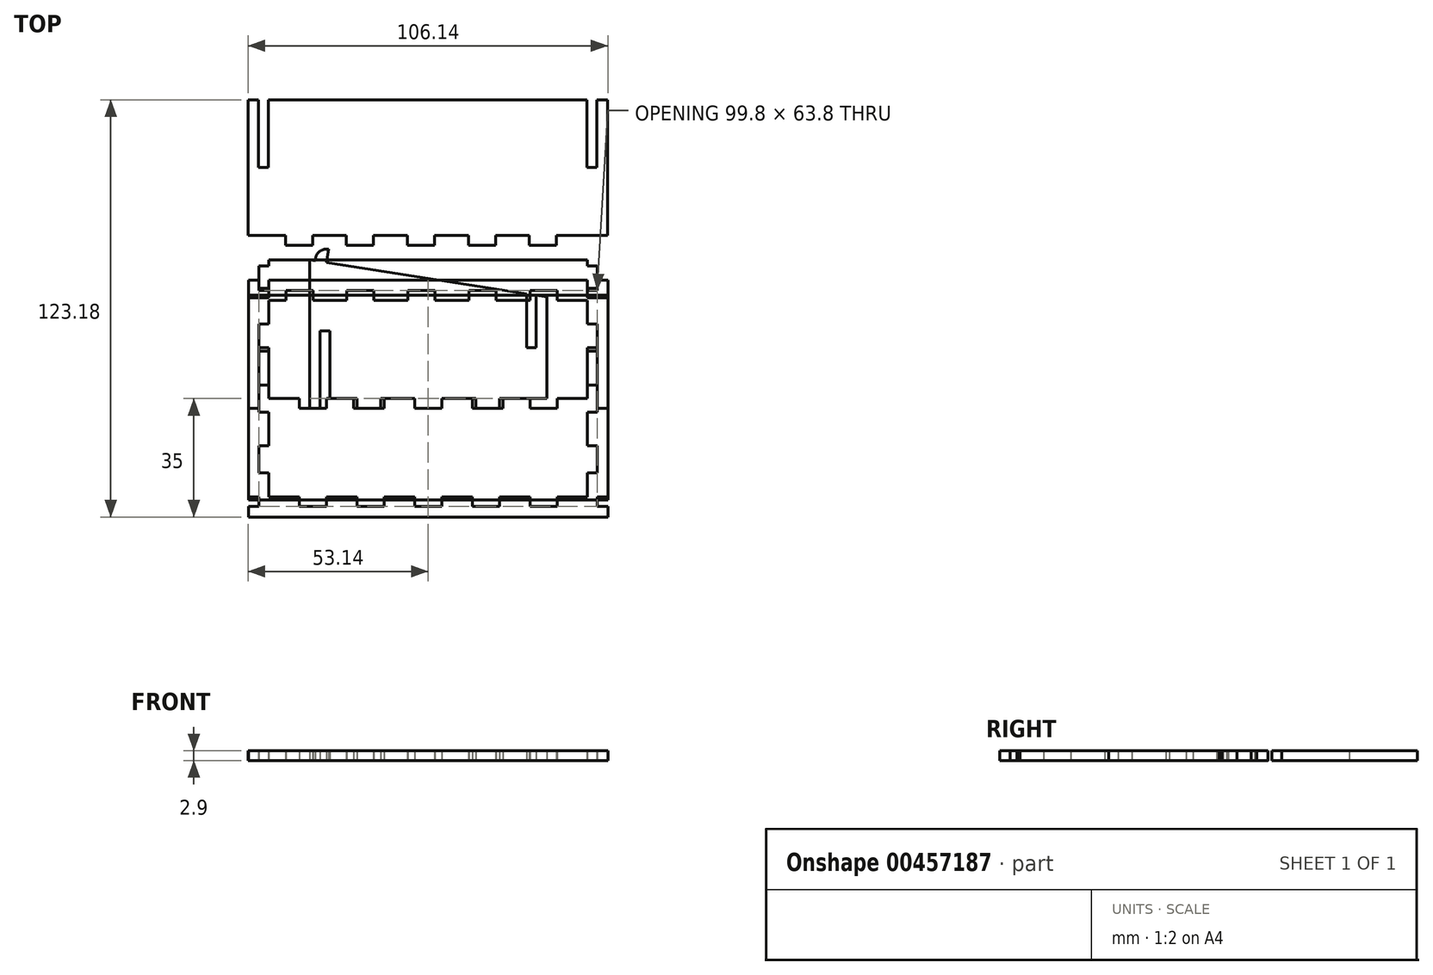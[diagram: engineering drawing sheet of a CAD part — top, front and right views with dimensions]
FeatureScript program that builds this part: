
annotation { "Feature Type Name" : "Feature", "Feature Type Description" : "" }
export const myFeature = defineFeature(function(context is Context, id is Id, definition is map)
    precondition{}
    {
        {
            assignVariable(context, id + "F0", {"name" : "b_thickness", "anyValue" : 2.9});
        }
        {
            var Q0;
            Q0=qCreatedBy(makeId("Top.planeOp"),FACE);
            var sketch = newSketch(context, id + "F1", { "sketchPlane" : qUnion([Q0])});
            skLineSegment(sketch, "E0", {"start": v(47, 29) * mm, "end": v(-47, 29) * mm});
            skLineSegment(sketch, "E1", {"start": v(-47, 29) * mm, "end": v(-47, -29) * mm});
            skLineSegment(sketch, "E2", {"start": v(-47, -29) * mm, "end": v(47, -29) * mm});
            skLineSegment(sketch, "E3", {"start": v(47, -29) * mm, "end": v(47, 29) * mm});
            skLineSegment(sketch, "E4", {"start": v(47, 29) * mm, "end": v(-47, -29) * mm});
            skLineSegment(sketch, "E5", {"start": v(-47, 29) * mm, "end": v(47, -29) * mm});
            skLineSegment(sketch, "E6", {"start": v(-47, 22) * mm, "end": v(-49.9, 22) * mm});
            skLineSegment(sketch, "E7", {"start": v(-49.9, 22) * mm, "end": v(-49.9, 14) * mm});
            skLineSegment(sketch, "E8", {"start": v(-49.9, 14) * mm, "end": v(-47, 14) * mm});
            skLineSegment(sketch, "E9", {"start": v(-47, 14) * mm, "end": v(-47, 22) * mm});
            skLineSegment(sketch, "E10", {"start": v(-47, -4) * mm, "end": v(-47, 4) * mm});
            skLineSegment(sketch, "E11", {"start": v(-47, 4) * mm, "end": v(-49.9, 4) * mm});
            skLineSegment(sketch, "E12", {"start": v(-49.9, 4) * mm, "end": v(-49.9, -4) * mm});
            skLineSegment(sketch, "E13", {"start": v(-49.9, -4) * mm, "end": v(-47, -4) * mm});
            skLineSegment(sketch, "E14", {"start": v(-47, -22) * mm, "end": v(-47, -14) * mm});
            skLineSegment(sketch, "E15", {"start": v(-47, -14) * mm, "end": v(-49.9, -14) * mm});
            skLineSegment(sketch, "E16", {"start": v(-49.9, -14) * mm, "end": v(-49.9, -22) * mm});
            skLineSegment(sketch, "E17", {"start": v(-49.9, -22) * mm, "end": v(-47, -22) * mm});
            skLineSegment(sketch, "E18", {"start": v(47, -14) * mm, "end": v(47, -22) * mm});
            skLineSegment(sketch, "E19", {"start": v(47, -22) * mm, "end": v(49.9, -22) * mm});
            skLineSegment(sketch, "E20", {"start": v(49.9, -22) * mm, "end": v(49.9, -14) * mm});
            skLineSegment(sketch, "E21", {"start": v(49.9, -14) * mm, "end": v(47, -14) * mm});
            skLineSegment(sketch, "E22", {"start": v(47, 4) * mm, "end": v(47, -4) * mm});
            skLineSegment(sketch, "E23", {"start": v(47, -4) * mm, "end": v(49.9, -4) * mm});
            skLineSegment(sketch, "E24", {"start": v(49.9, -4) * mm, "end": v(49.9, 4) * mm});
            skLineSegment(sketch, "E25", {"start": v(49.9, 4) * mm, "end": v(47, 4) * mm});
            skLineSegment(sketch, "E26", {"start": v(47, 22) * mm, "end": v(47, 14) * mm});
            skLineSegment(sketch, "E27", {"start": v(47, 14) * mm, "end": v(49.9, 14) * mm});
            skLineSegment(sketch, "E28", {"start": v(49.9, 14) * mm, "end": v(49.9, 22) * mm});
            skLineSegment(sketch, "E29", {"start": v(49.9, 22) * mm, "end": v(47, 22) * mm});
            skLineSegment(sketch, "E30", {"start": v(-30, -29) * mm, "end": v(-38, -29) * mm});
            skLineSegment(sketch, "E31", {"start": v(-38, -29) * mm, "end": v(-38, -31.9) * mm});
            skLineSegment(sketch, "E32", {"start": v(-38, -31.9) * mm, "end": v(-30, -31.9) * mm});
            skLineSegment(sketch, "E33", {"start": v(-30, -31.9) * mm, "end": v(-30, -29) * mm});
            skLineSegment(sketch, "E34", {"start": v(-13, -29) * mm, "end": v(-21, -29) * mm});
            skLineSegment(sketch, "E35", {"start": v(-21, -29) * mm, "end": v(-21, -31.9) * mm});
            skLineSegment(sketch, "E36", {"start": v(-21, -31.9) * mm, "end": v(-13, -31.9) * mm});
            skLineSegment(sketch, "E37", {"start": v(-13, -31.9) * mm, "end": v(-13, -29) * mm});
            skLineSegment(sketch, "E38", {"start": v(4, -29) * mm, "end": v(-4, -29) * mm});
            skLineSegment(sketch, "E39", {"start": v(-4, -29) * mm, "end": v(-4, -31.9) * mm});
            skLineSegment(sketch, "E40", {"start": v(-4, -31.9) * mm, "end": v(4, -31.9) * mm});
            skLineSegment(sketch, "E41", {"start": v(4, -31.9) * mm, "end": v(4, -29) * mm});
            skLineSegment(sketch, "E42", {"start": v(21, -29) * mm, "end": v(13, -29) * mm});
            skLineSegment(sketch, "E43", {"start": v(13, -29) * mm, "end": v(13, -31.9) * mm});
            skLineSegment(sketch, "E44", {"start": v(13, -31.9) * mm, "end": v(21, -31.9) * mm});
            skLineSegment(sketch, "E45", {"start": v(21, -31.9) * mm, "end": v(21, -29) * mm});
            skLineSegment(sketch, "E46", {"start": v(38, -29) * mm, "end": v(30, -29) * mm});
            skLineSegment(sketch, "E47", {"start": v(30, -29) * mm, "end": v(30, -31.9) * mm});
            skLineSegment(sketch, "E48", {"start": v(30, -31.9) * mm, "end": v(38, -31.9) * mm});
            skLineSegment(sketch, "E49", {"start": v(38, -31.9) * mm, "end": v(38, -29) * mm});
            skLineSegment(sketch, "E50", {"start": v(30, 29) * mm, "end": v(38, 29) * mm});
            skLineSegment(sketch, "E51", {"start": v(38, 29) * mm, "end": v(38, 31.9) * mm});
            skLineSegment(sketch, "E52", {"start": v(38, 31.9) * mm, "end": v(30, 31.9) * mm});
            skLineSegment(sketch, "E53", {"start": v(30, 31.9) * mm, "end": v(30, 29) * mm});
            skLineSegment(sketch, "E54", {"start": v(12, 29) * mm, "end": v(20, 29) * mm});
            skLineSegment(sketch, "E55", {"start": v(20, 29) * mm, "end": v(20, 31.9) * mm});
            skLineSegment(sketch, "E56", {"start": v(20, 31.9) * mm, "end": v(12, 31.9) * mm});
            skLineSegment(sketch, "E57", {"start": v(12, 31.9) * mm, "end": v(12, 29) * mm});
            skLineSegment(sketch, "E58", {"start": v(-6, 29) * mm, "end": v(2, 29) * mm});
            skLineSegment(sketch, "E59", {"start": v(2, 29) * mm, "end": v(2, 31.9) * mm});
            skLineSegment(sketch, "E60", {"start": v(2, 31.9) * mm, "end": v(-6, 31.9) * mm});
            skLineSegment(sketch, "E61", {"start": v(-6, 31.9) * mm, "end": v(-6, 29) * mm});
            skLineSegment(sketch, "E62", {"start": v(-24, 29) * mm, "end": v(-16, 29) * mm});
            skLineSegment(sketch, "E63", {"start": v(-16, 29) * mm, "end": v(-16, 31.9) * mm});
            skLineSegment(sketch, "E64", {"start": v(-16, 31.9) * mm, "end": v(-24, 31.9) * mm});
            skLineSegment(sketch, "E65", {"start": v(-24, 31.9) * mm, "end": v(-24, 29) * mm});
            skLineSegment(sketch, "E66", {"start": v(-42, 29) * mm, "end": v(-34, 29) * mm});
            skLineSegment(sketch, "E67", {"start": v(-34, 29) * mm, "end": v(-34, 31.9) * mm});
            skLineSegment(sketch, "E68", {"start": v(-34, 31.9) * mm, "end": v(-42, 31.9) * mm});
            skLineSegment(sketch, "E69", {"start": v(-42, 31.9) * mm, "end": v(-42, 29) * mm});
            skLineSegment(sketch, "E70", {"start": v(-53, -35) * mm, "end": v(-53, 35) * mm});
            skLineSegment(sketch, "E71", {"start": v(-53, 35) * mm, "end": v(53, 35) * mm});
            skLineSegment(sketch, "E72", {"start": v(53, 35) * mm, "end": v(53, -35) * mm});
            skLineSegment(sketch, "E73", {"start": v(53, -35) * mm, "end": v(-53, -35) * mm});
            skLineSegment(sketch, "E74", {"start": v(-49.9, 35) * mm, "end": v(-49.9, 31.9) * mm});
            skLineSegment(sketch, "E75", {"start": v(-49.9, 31.9) * mm, "end": v(-47, 31.9) * mm});
            skLineSegment(sketch, "E76", {"start": v(-47, 31.9) * mm, "end": v(-47, 35) * mm});
            skLineSegment(sketch, "E77", {"start": v(49.9, 35) * mm, "end": v(49.9, 31.9) * mm});
            skLineSegment(sketch, "E78", {"start": v(49.9, 31.9) * mm, "end": v(47, 31.9) * mm});
            skLineSegment(sketch, "E79", {"start": v(47, 31.9) * mm, "end": v(47, 35) * mm});
            skLineSegment(sketch, "E80", {"start": v(-53, -31.9) * mm, "end": v(-49.9, -31.9) * mm});
            skLineSegment(sketch, "E81", {"start": v(-49.9, -31.9) * mm, "end": v(-49.9, -29) * mm});
            skLineSegment(sketch, "E82", {"start": v(-49.9, -29) * mm, "end": v(-53, -29) * mm});
            skLineSegment(sketch, "E83", {"start": v(53, -31.9) * mm, "end": v(49.9, -31.9) * mm});
            skLineSegment(sketch, "E84", {"start": v(49.9, -31.9) * mm, "end": v(49.9, -29) * mm});
            skLineSegment(sketch, "E85", {"start": v(49.9, -29) * mm, "end": v(53, -29) * mm});
            skSolve(sketch);
        }
        {
            var Q0;
            {var subQ1=sQuery(id+"F1.wireOp",EDGE,"E30");Q0=makeQuery(id+"F1.imprint","IMPRINT",FACE,{"disambiguationData":[TD([[makeQuery(id+"F1.imprint","IMPRINT",EDGE,{"derivedFrom":subQ1}),-1.0]])]});}
            var Q1;
            {var subQ5=sQuery(id+"F1.wireOp",EDGE,"E9");Q1=makeQuery(id+"F1.imprint","IMPRINT",FACE,{"disambiguationData":[TD([[makeQuery(id+"F1.imprint","IMPRINT",EDGE,{"derivedFrom":subQ5}),-1.0]])]});}
            var Q2;
            {var subQ10=sQuery(id+"F1.wireOp",EDGE,"E50");Q2=makeQuery(id+"F1.imprint","IMPRINT",FACE,{"disambiguationData":[TD([[makeQuery(id+"F1.imprint","IMPRINT",EDGE,{"derivedFrom":subQ10}),-1.0]])]});}
            var Q3;
            {var subQ5=sQuery(id+"F1.wireOp",EDGE,"E18");Q3=makeQuery(id+"F1.imprint","IMPRINT",FACE,{"disambiguationData":[TD([[makeQuery(id+"F1.imprint","IMPRINT",EDGE,{"derivedFrom":subQ5}),-1.0]])]});}
            var Q4;
            {var subQ24=sQuery(id+"F1.wireOp",EDGE,"E6");Q4=makeQuery(id+"F1.imprint","IMPRINT",FACE,{"disambiguationData":[TD([[makeQuery(id+"F1.imprint","IMPRINT",EDGE,{"derivedFrom":subQ24}),-1.0]])]});}
            extrude(context, id + "F2", {"entities" : qUnion([Q0, Q1, Q2, Q3, Q4]), "depth" : getVariable(context, 'b_thickness') * mm});
        }
        {
            var Q0;
            Q0=qCreatedBy(makeId("Top.planeOp"),FACE);
            var sketch = newSketch(context, id + "F3", { "sketchPlane" : qUnion([Q0])});
            skLineSegment(sketch, "E86.MirrorCS", {"start": v(52.86, 48.18) * mm, "end": v(52.86, 88.18) * mm});
            skLineSegment(sketch, "E87.MirrorCS", {"start": v(49.76, 88.18) * mm, "end": v(49.76, 68.18) * mm});
            skLineSegment(sketch, "E88.MirrorCS", {"start": v(52.86, 88.18) * mm, "end": v(49.76, 88.18) * mm});
            skLineSegment(sketch, "E89.MirrorCS", {"start": v(52.86, 68.18) * mm, "end": v(-53.14, 68.18) * mm});
            skLineSegment(sketch, "E90.MirrorCS", {"start": v(52.86, 48.18) * mm, "end": v(37.86, 48.18) * mm});
            skLineSegment(sketch, "E91.MirrorCS", {"start": v(29.86, 48.18) * mm, "end": v(19.86, 48.18) * mm});
            skLineSegment(sketch, "E92.MirrorCS", {"start": v(11.86, 48.18) * mm, "end": v(1.86, 48.18) * mm});
            skLineSegment(sketch, "E93.MirrorCS", {"start": v(-6.14, 48.18) * mm, "end": v(-16.14, 48.18) * mm});
            skLineSegment(sketch, "E94.MirrorCS", {"start": v(-24.14, 48.18) * mm, "end": v(-34.14, 48.18) * mm});
            skLineSegment(sketch, "E95.MirrorCS", {"start": v(-42.14, 48.18) * mm, "end": v(-53.14, 48.18) * mm});
            skLineSegment(sketch, "E96.MirrorCS", {"start": v(-53.14, 48.18) * mm, "end": v(-53.14, 88.18) * mm});
            skLineSegment(sketch, "E97.MirrorCS", {"start": v(-50.04, 88.18) * mm, "end": v(-50.04, 68.18) * mm});
            skLineSegment(sketch, "E98.MirrorCS", {"start": v(-47.14, 84.18) * mm, "end": v(-47.14, 68.18) * mm});
            skLineSegment(sketch, "E99.MirrorCS", {"start": v(-47.14, 84.18) * mm, "end": v(46.86, 84.18) * mm});
            skLineSegment(sketch, "E100.MirrorCS", {"start": v(46.86, 88.18) * mm, "end": v(-47.14, 88.18) * mm});
            skLineSegment(sketch, "E101.MirrorCS", {"start": v(46.86, 84.18) * mm, "end": v(46.86, 68.18) * mm});
            skLineSegment(sketch, "E102.MirrorCS", {"start": v(46.86, 88.18) * mm, "end": v(46.86, 84.18) * mm});
            skLineSegment(sketch, "E103.MirrorCS", {"start": v(-47.14, 88.18) * mm, "end": v(-47.14, 84.18) * mm});
            skLineSegment(sketch, "E104.MirrorCS", {"start": v(-50.04, 88.18) * mm, "end": v(-53.14, 88.18) * mm});
            skLineSegment(sketch, "E105.MirrorCS", {"start": v(-34.14, 45.28) * mm, "end": v(-42.14, 45.28) * mm});
            skLineSegment(sketch, "E106.MirrorCS", {"start": v(-16.14, 45.28) * mm, "end": v(-24.14, 45.28) * mm});
            skLineSegment(sketch, "E107.MirrorCS", {"start": v(1.86, 45.28) * mm, "end": v(-6.14, 45.28) * mm});
            skLineSegment(sketch, "E108.MirrorCS", {"start": v(19.86, 45.28) * mm, "end": v(11.86, 45.28) * mm});
            skLineSegment(sketch, "E109.MirrorCS", {"start": v(37.86, 45.28) * mm, "end": v(29.86, 45.28) * mm});
            skLineSegment(sketch, "E110.MirrorCS", {"start": v(37.86, 48.18) * mm, "end": v(37.86, 45.28) * mm});
            skLineSegment(sketch, "E111.MirrorCS", {"start": v(29.86, 45.28) * mm, "end": v(29.86, 48.18) * mm});
            skLineSegment(sketch, "E112.MirrorCS", {"start": v(19.86, 48.18) * mm, "end": v(19.86, 45.28) * mm});
            skLineSegment(sketch, "E113.MirrorCS", {"start": v(11.86, 45.28) * mm, "end": v(11.86, 48.18) * mm});
            skLineSegment(sketch, "E114.MirrorCS", {"start": v(-6.14, 45.28) * mm, "end": v(-6.14, 48.18) * mm});
            skLineSegment(sketch, "E115.MirrorCS", {"start": v(-16.14, 48.18) * mm, "end": v(-16.14, 45.28) * mm});
            skLineSegment(sketch, "E116.MirrorCS", {"start": v(-24.14, 45.28) * mm, "end": v(-24.14, 48.18) * mm});
            skLineSegment(sketch, "E117.MirrorCS", {"start": v(-34.14, 48.18) * mm, "end": v(-34.14, 45.28) * mm});
            skLineSegment(sketch, "E118.MirrorCS", {"start": v(-42.14, 45.28) * mm, "end": v(-42.14, 48.18) * mm});
            skLineSegment(sketch, "E119.MirrorCS", {"start": v(1.86, 48.18) * mm, "end": v(1.86, 45.28) * mm});
            skSolve(sketch);
        }
        {
            var Q0;
            {var subQ0=sQuery(id+"F3.wireOp",EDGE,"E98.MirrorCS");Q0=makeQuery(id+"F3.imprint","IMPRINT",FACE,{"disambiguationData":[TD([[makeQuery(id+"F3.imprint","IMPRINT",EDGE,{"derivedFrom":subQ0}),1.0]])]});}
            var Q1;
            Q1=makeQuery(id+"F3.imprint","IMPRINT",FACE,{"disambiguationData":[TD([[makeQuery(id+"F3.imprint","IMPRINT",EDGE,{"derivedFrom":sQuery(id+"F3.wireOp",EDGE,"E99.MirrorCS")}),1.0]])]});
            var Q2;
            {var subQ3=sQuery(id+"F3.wireOp",EDGE,"E97.MirrorCS");Q2=makeQuery(id+"F3.imprint","IMPRINT",FACE,{"disambiguationData":[TD([[makeQuery(id+"F3.imprint","IMPRINT",EDGE,{"derivedFrom":subQ3}),-1.0]])]});}
            var Q3;
            {var subQ9=sQuery(id+"F3.wireOp",EDGE,"E90.MirrorCS");Q3=makeQuery(id+"F3.imprint","IMPRINT",FACE,{"disambiguationData":[TD([[makeQuery(id+"F3.imprint","IMPRINT",EDGE,{"derivedFrom":subQ9}),-1.0]])]});}
            var Q4;
            {var subQ4=sQuery(id+"F3.wireOp",EDGE,"E87.MirrorCS");Q4=makeQuery(id+"F3.imprint","IMPRINT",FACE,{"disambiguationData":[TD([[makeQuery(id+"F3.imprint","IMPRINT",EDGE,{"derivedFrom":subQ4}),1.0]])]});}
            extrude(context, id + "F4", {"entities" : qUnion([Q0, Q1, Q2, Q3, Q4]), "depth" : getVariable(context, 'b_thickness') * mm});
        }
        {
            var Q0;
            Q0=qCreatedBy(makeId("Top.planeOp"),FACE);
            var sketch = newSketch(context, id + "F5", { "sketchPlane" : qUnion([Q0])});
            skLineSegment(sketch, "E120", {"start": v(-22, 0) * mm, "end": v(-22, -2.9) * mm});
            skLineSegment(sketch, "E121", {"start": v(-22, -2.9) * mm, "end": v(-14, -2.9) * mm});
            skLineSegment(sketch, "E122", {"start": v(-14, -2.9) * mm, "end": v(-14, 0) * mm});
            skLineSegment(sketch, "E123", {"start": v(-14, 0) * mm, "end": v(-4, 0) * mm});
            skLineSegment(sketch, "E124", {"start": v(-4, 0) * mm, "end": v(-4, -2.9) * mm});
            skLineSegment(sketch, "E125", {"start": v(-4, -2.9) * mm, "end": v(4, -2.9) * mm});
            skLineSegment(sketch, "E126", {"start": v(4, -2.9) * mm, "end": v(4, 0) * mm});
            skLineSegment(sketch, "E127", {"start": v(4, 0) * mm, "end": v(14, 0) * mm});
            skLineSegment(sketch, "E128", {"start": v(14, 0) * mm, "end": v(14, -2.9) * mm});
            skLineSegment(sketch, "E129", {"start": v(14, -2.9) * mm, "end": v(22, -2.9) * mm});
            skLineSegment(sketch, "E130", {"start": v(22, -2.9) * mm, "end": v(22, 0) * mm});
            skLineSegment(sketch, "E131", {"start": v(35, 0) * mm, "end": v(35, 30) * mm});
            skLineSegment(sketch, "E132", {"start": v(35, 30) * mm, "end": v(-29, 40) * mm});
            skLineSegment(sketch, "E133", {"start": v(-31.9, 20) * mm, "end": v(-29, 20) * mm});
            skLineSegment(sketch, "E134", {"start": v(-29, 20) * mm, "end": v(-29, 0) * mm});
            skLineSegment(sketch, "E135", {"start": v(-22, 0) * mm, "end": v(-29, 0) * mm});
            skLineSegment(sketch, "E136", {"start": v(-35, 40.94) * mm, "end": v(-35, -2.9) * mm});
            skLineSegment(sketch, "E137", {"start": v(-35, -2.9) * mm, "end": v(-31.9, -2.9) * mm});
            skLineSegment(sketch, "E138", {"start": v(-31.9, -2.9) * mm, "end": v(-31.9, 20) * mm});
            skLineSegment(sketch, "E139", {"start": v(35, 15) * mm, "end": v(-29, 15) * mm});
            skLineSegment(sketch, "E140", {"start": v(31.9, 15) * mm, "end": v(29, 15) * mm});
            skLineSegment(sketch, "E141", {"start": v(22, 0) * mm, "end": v(35, 0) * mm});
            skLineSegment(sketch, "E142", {"start": v(31.9, 30.48) * mm, "end": v(31.9, 15) * mm});
            skLineSegment(sketch, "E143", {"start": v(29, 15) * mm, "end": v(29, 30.94) * mm});
            skLineSegment(sketch, "E144", {"start": v(-29, 40) * mm, "end": v(-35, 40.94) * mm});
            skArc(sketch, "E145", {"start": v(-25, 39.38) * mm, "mid": v(-29.09, 46) * mm, "end": v(-35, 40.94) * mm});
            skLineSegment(sketch, "E146", {"start": v(-30, 40.16) * mm, "end": v(-29.38, 44.1) * mm});
            skArc(sketch, "E147", {"start": v(-33.31, 40.67) * mm, "mid": v(-29.38, 44.1) * mm, "end": v(-26.69, 39.64) * mm});
            skLineSegment(sketch, "E148", {"start": v(-26.69, 39.64) * mm, "end": v(-33.31, 40.67) * mm});
            skSolve(sketch);
        }
        {
            var Q0;
            {var subQ10=sQuery(id+"F5.wireOp",EDGE,"E133");Q0=makeQuery(id+"F5.imprint","IMPRINT",FACE,{"disambiguationData":[TD([[makeQuery(id+"F5.imprint","IMPRINT",EDGE,{"derivedFrom":subQ10}),1.0]])]});}
            var Q1;
            Q1=makeQuery(id+"F5.imprint","IMPRINT",FACE,{"disambiguationData":[TD([[makeQuery(id+"F5.imprint","IMPRINT",EDGE,{"derivedFrom":sQuery(id+"F5.wireOp",EDGE,"E120")}),1.0]])]});
            var Q2;
            {var subQ5=sQuery(id+"F5.wireOp",EDGE,"E142");Q2=makeQuery(id+"F5.imprint","IMPRINT",FACE,{"disambiguationData":[TD([[makeQuery(id+"F5.imprint","IMPRINT",EDGE,{"derivedFrom":subQ5}),1.0]])]});}
            var Q3;
            {var subQ2=sQuery(id+"F5.wireOp",EDGE,"E144");Q3=makeQuery(id+"F5.imprint","IMPRINT",FACE,{"disambiguationData":[TD([[makeQuery(id+"F5.imprint","IMPRINT",EDGE,{"derivedFrom":subQ2}),-1.0]])]});}
            extrude(context, id + "F6", {"entities" : qUnion([Q0, Q1, Q2, Q3]), "depth" : getVariable(context, 'b_thickness') * mm});
        }
        {
            var Q0;
            Q0=qCreatedBy(makeId("Top.planeOp"),FACE);
            var sketch = newSketch(context, id + "F7", { "sketchPlane" : qUnion([Q0])});
            skLineSegment(sketch, "E149", {"start": v(-38, 0) * mm, "end": v(-38, -2.9) * mm});
            skLineSegment(sketch, "E150", {"start": v(-38, -2.9) * mm, "end": v(-30, -2.9) * mm});
            skLineSegment(sketch, "E151", {"start": v(-30, -2.9) * mm, "end": v(-30, 0) * mm});
            skLineSegment(sketch, "E152", {"start": v(-30, 0) * mm, "end": v(-21, 0) * mm});
            skLineSegment(sketch, "E153", {"start": v(-21, 0) * mm, "end": v(-21, -2.9) * mm});
            skLineSegment(sketch, "E154", {"start": v(-21, -2.9) * mm, "end": v(-13, -2.9) * mm});
            skLineSegment(sketch, "E155", {"start": v(-13, -2.9) * mm, "end": v(-13, 0) * mm});
            skLineSegment(sketch, "E156", {"start": v(-13, 0) * mm, "end": v(-4, 0) * mm});
            skLineSegment(sketch, "E157", {"start": v(-4, 0) * mm, "end": v(-4, -2.9) * mm});
            skLineSegment(sketch, "E158", {"start": v(-4, -2.9) * mm, "end": v(4, -2.9) * mm});
            skLineSegment(sketch, "E159", {"start": v(4, -2.9) * mm, "end": v(4, 0) * mm});
            skLineSegment(sketch, "E160", {"start": v(4, 0) * mm, "end": v(13, 0) * mm});
            skLineSegment(sketch, "E161", {"start": v(13, 0) * mm, "end": v(13, -2.9) * mm});
            skLineSegment(sketch, "E162", {"start": v(13, -2.9) * mm, "end": v(21, -2.9) * mm});
            skLineSegment(sketch, "E163", {"start": v(21, -2.9) * mm, "end": v(21, 0) * mm});
            skLineSegment(sketch, "E164", {"start": v(21, 0) * mm, "end": v(30, 0) * mm});
            skLineSegment(sketch, "E165", {"start": v(30, 0) * mm, "end": v(30, -2.9) * mm});
            skLineSegment(sketch, "E166", {"start": v(30, -2.9) * mm, "end": v(38, -2.9) * mm});
            skLineSegment(sketch, "E167", {"start": v(38, -2.9) * mm, "end": v(38, 0) * mm});
            skLineSegment(sketch, "E168", {"start": v(-53, 30.5) * mm, "end": v(53, 30.5) * mm});
            skLineSegment(sketch, "E169", {"start": v(0, 30.5) * mm, "end": v(0, 0) * mm});
            skLineSegment(sketch, "E170", {"start": v(-9, 30.5) * mm, "end": v(-9, 11) * mm});
            skLineSegment(sketch, "E171", {"start": v(-5, 7) * mm, "end": v(5, 7) * mm});
            skLineSegment(sketch, "E172", {"start": v(9, 11) * mm, "end": v(9, 30.5) * mm});
            skArc(sketch, "E173", {"start": v(-9, 11) * mm, "mid": v(-7.83, 8.17) * mm, "end": v(-5, 7) * mm});
            skArc(sketch, "E174", {"start": v(5, 7) * mm, "mid": v(7.83, 8.17) * mm, "end": v(9, 11) * mm});
            skLineSegment(sketch, "E175", {"start": v(-53, -2.9) * mm, "end": v(-53, 30.5) * mm});
            skLineSegment(sketch, "E176", {"start": v(-53, -2.9) * mm, "end": v(-49.9, -2.9) * mm});
            skLineSegment(sketch, "E177", {"start": v(-49.9, -2.9) * mm, "end": v(-49.9, 15) * mm});
            skLineSegment(sketch, "E178", {"start": v(-49.9, 15) * mm, "end": v(-47, 15) * mm});
            skLineSegment(sketch, "E179", {"start": v(-47, 15) * mm, "end": v(-47, 0) * mm});
            skLineSegment(sketch, "E180", {"start": v(-47, 0) * mm, "end": v(-38, 0) * mm});
            skLineSegment(sketch, "E181", {"start": v(53, 30.5) * mm, "end": v(53, -2.9) * mm});
            skLineSegment(sketch, "E182", {"start": v(47, 15) * mm, "end": v(47, 0) * mm});
            skLineSegment(sketch, "E183", {"start": v(47, 0) * mm, "end": v(38, 0) * mm});
            skLineSegment(sketch, "E184", {"start": v(47, 15) * mm, "end": v(49.9, 15) * mm});
            skLineSegment(sketch, "E185", {"start": v(49.9, 15) * mm, "end": v(49.9, -2.9) * mm});
            skLineSegment(sketch, "E186", {"start": v(49.9, -2.9) * mm, "end": v(53, -2.9) * mm});
            skSolve(sketch);
        }
        {
            var Q0;
            Q0 = qSketchRegion(id + "F7", true);
            extrude(context, id + "F8", {"entities" : qUnion([Q0]), "depth" : getVariable(context, 'b_thickness') * mm});
        }
        {
            var Q0;
            Q0=qCreatedBy(makeId("Top.planeOp"),FACE);
            var sketch = newSketch(context, id + "F9", { "sketchPlane" : qUnion([Q0])});
            skLineSegment(sketch, "E187", {"start": v(47, 40.9) * mm, "end": v(-47, 40.9) * mm});
            skLineSegment(sketch, "E188", {"start": v(53, -29.95) * mm, "end": v(-53, -29.95) * mm});
            skLineSegment(sketch, "E189", {"start": v(-53, -29.95) * mm, "end": v(-53, 29.78) * mm});
            skLineSegment(sketch, "E190", {"start": v(53, -29.95) * mm, "end": v(53, 29.78) * mm});
            skLineSegment(sketch, "E191", {"start": v(-47, 30.78) * mm, "end": v(47, 30.78) * mm});
            skLineSegment(sketch, "E192", {"start": v(-53, 29.78) * mm, "end": v(-47, 29.78) * mm});
            skLineSegment(sketch, "E193", {"start": v(47, 29.78) * mm, "end": v(53, 29.78) * mm});
            skLineSegment(sketch, "E194", {"start": v(-47, 29.78) * mm, "end": v(47, 29.78) * mm});
            skLineSegment(sketch, "E195", {"start": v(-47, 39.2) * mm, "end": v(-49.92, 39.18) * mm});
            skLineSegment(sketch, "E196", {"start": v(-49.9, 32.48) * mm, "end": v(-47, 32.49) * mm});
            skLineSegment(sketch, "E197", {"start": v(-49.9, 32.48) * mm, "end": v(-49.92, 39.18) * mm});
            skLineSegment(sketch, "E198", {"start": v(-47, 37.2) * mm, "end": v(-49.92, 37.18) * mm});
            skLineSegment(sketch, "E199", {"start": v(-47, 34.49) * mm, "end": v(-49.91, 34.48) * mm});
            skLineSegment(sketch, "E200", {"start": v(-47, 40.9) * mm, "end": v(-47, 37.2) * mm});
            skLineSegment(sketch, "E201", {"start": v(-47, 34.49) * mm, "end": v(-47, 29.78) * mm});
            skLineSegment(sketch, "E202", {"start": v(-47, 37.2) * mm, "end": v(-47, 34.49) * mm});
            skLineSegment(sketch, "E203", {"start": v(47, 39.2) * mm, "end": v(49.92, 39.18) * mm});
            skLineSegment(sketch, "E204", {"start": v(49.92, 39.18) * mm, "end": v(49.9, 32.48) * mm});
            skLineSegment(sketch, "E205", {"start": v(49.9, 32.48) * mm, "end": v(47, 32.49) * mm});
            skLineSegment(sketch, "E206", {"start": v(47, 34.49) * mm, "end": v(49.91, 34.48) * mm});
            skLineSegment(sketch, "E207", {"start": v(47, 37.2) * mm, "end": v(49.92, 37.18) * mm});
            skLineSegment(sketch, "E208", {"start": v(47, 40.9) * mm, "end": v(47, 37.2) * mm});
            skLineSegment(sketch, "E209", {"start": v(47, 34.49) * mm, "end": v(47, 29.78) * mm});
            skLineSegment(sketch, "E210", {"start": v(47, 37.2) * mm, "end": v(47, 34.49) * mm});
            skSolve(sketch);
        }
        {
            var Q0;
            {var subQ0=sQuery(id+"F9.wireOp",EDGE,"E206");Q0=makeQuery(id+"F9.imprint","IMPRINT",FACE,{"disambiguationData":[TD([[makeQuery(id+"F9.imprint","IMPRINT",EDGE,{"derivedFrom":subQ0}),1.0]])]});}
            var Q1;
            {var subQ0=sQuery(id+"F9.wireOp",EDGE,"E195");Q1=makeQuery(id+"F9.imprint","IMPRINT",FACE,{"disambiguationData":[TD([[makeQuery(id+"F9.imprint","IMPRINT",EDGE,{"derivedFrom":subQ0}),1.0]])]});}
            var Q2;
            {var subQ9=sQuery(id+"F9.wireOp",EDGE,"E187");Q2=makeQuery(id+"F9.imprint","IMPRINT",FACE,{"disambiguationData":[TD([[makeQuery(id+"F9.imprint","IMPRINT",EDGE,{"derivedFrom":subQ9}),1.0]])]});}
            var Q3;
            Q3=makeQuery(id+"F9.imprint","IMPRINT",FACE,{"disambiguationData":[TD([[makeQuery(id+"F9.imprint","IMPRINT",EDGE,{"derivedFrom":sQuery(id+"F9.wireOp",EDGE,"E188")}),-1.0]])]});
            var Q4;
            {var subQ0=sQuery(id+"F9.wireOp",EDGE,"E191");Q4=makeQuery(id+"F9.imprint","IMPRINT",FACE,{"disambiguationData":[TD([[makeQuery(id+"F9.imprint","IMPRINT",EDGE,{"derivedFrom":subQ0}),-1.0]])]});}
            var Q5;
            {var subQ0=sQuery(id+"F9.wireOp",EDGE,"E198");Q5=makeQuery(id+"F9.imprint","IMPRINT",FACE,{"disambiguationData":[TD([[makeQuery(id+"F9.imprint","IMPRINT",EDGE,{"derivedFrom":subQ0}),1.0]])]});}
            var Q6;
            {var subQ0=sQuery(id+"F9.wireOp",EDGE,"E203");Q6=makeQuery(id+"F9.imprint","IMPRINT",FACE,{"disambiguationData":[TD([[makeQuery(id+"F9.imprint","IMPRINT",EDGE,{"derivedFrom":subQ0}),-1.0]])]});}
            var Q7;
            {var subQ0=sQuery(id+"F9.wireOp",EDGE,"E196");Q7=makeQuery(id+"F9.imprint","IMPRINT",FACE,{"disambiguationData":[TD([[makeQuery(id+"F9.imprint","IMPRINT",EDGE,{"derivedFrom":subQ0}),1.0]])]});}
            var Q8;
            {var subQ0=sQuery(id+"F9.wireOp",EDGE,"E205");Q8=makeQuery(id+"F9.imprint","IMPRINT",FACE,{"disambiguationData":[TD([[makeQuery(id+"F9.imprint","IMPRINT",EDGE,{"derivedFrom":subQ0}),-1.0]])]});}
            extrude(context, id + "F10", {"entities" : qUnion([Q0, Q1, Q2, Q3, Q4, Q5, Q6, Q7, Q8]), "depth" : getVariable(context, 'b_thickness') * mm});
        }
    });
